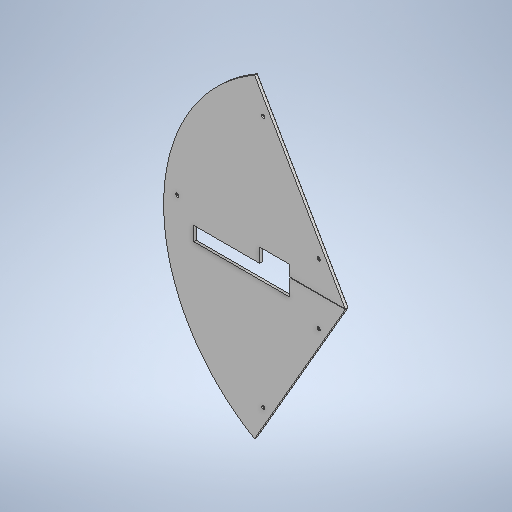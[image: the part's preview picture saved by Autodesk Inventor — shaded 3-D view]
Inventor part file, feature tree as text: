
AUTODESK INVENTOR PART (.ipt)
format: ipt  version: 2025.1 (Build 291241000, 241)  size: 319,488 bytes
history: native  units: mm
features: extrude x4, sketch x4, fillet x2, chamfer x1
ambient origin geometry x8: Origin, YZ Plane, XZ Plane, XY Plane, X Axis, Y Axis, Z Axis, Center Point
bodies: Volumenkörper1 (feature_tree)
feature tree (11):
  extrude  "Extrusion1"  TaperAngle=120.0deg  [1 undecoded]
  fillet  "Rundung1"  [1 undecoded]
  extrude  "Extrusion2"  Depth=0.5mm
  fillet  "Rundung2"  Radius=14.0mm
  extrude  "Extrusion3"  Depth=17.0mm
  extrude  "Extrusion4"  Depth=3.0mm TaperAngle=0.0deg
  chamfer  "Fasen1"  Distance=30.0mm
  sketch  "Skizze1"  dims[d0=360.0mm d1=120.0deg d2=60.0deg]
  sketch  "Skizze2"  dims[d3=3.0mm d4=0.0mm d5=0.5mm d6=14.0mm]
  sketch  "Skizze3"  dims[d7=95.0mm d8=17.0mm]
  sketch  "Skizze4"  dims[d10=150.0mm d11=3.0mm d12=0.0mm d13=30.0mm d14=14.0mm d15=0.5mm d16=0.5mm d17=0.25mm d18=60.0mm d19=0.0mm d20=3.0mm d21=0.0mm d26=26.558mm d27=26.558mm d28=3.3mm d29=81.406mm d30=81.406mm d31=14.8mm d32=166.5mm d33=125.0mm d34=30.0mm d35=30.0mm d36=125.0mm d37=3.0mm d38=0.0mm d39=1.9mm d40=2.0mm d41=45.0deg]
note: 2 required parameter values undecoded (feature->parameter linkage not recoverable at this tier; creation-order binding heuristic only, values carry confidence <= 0.55)
